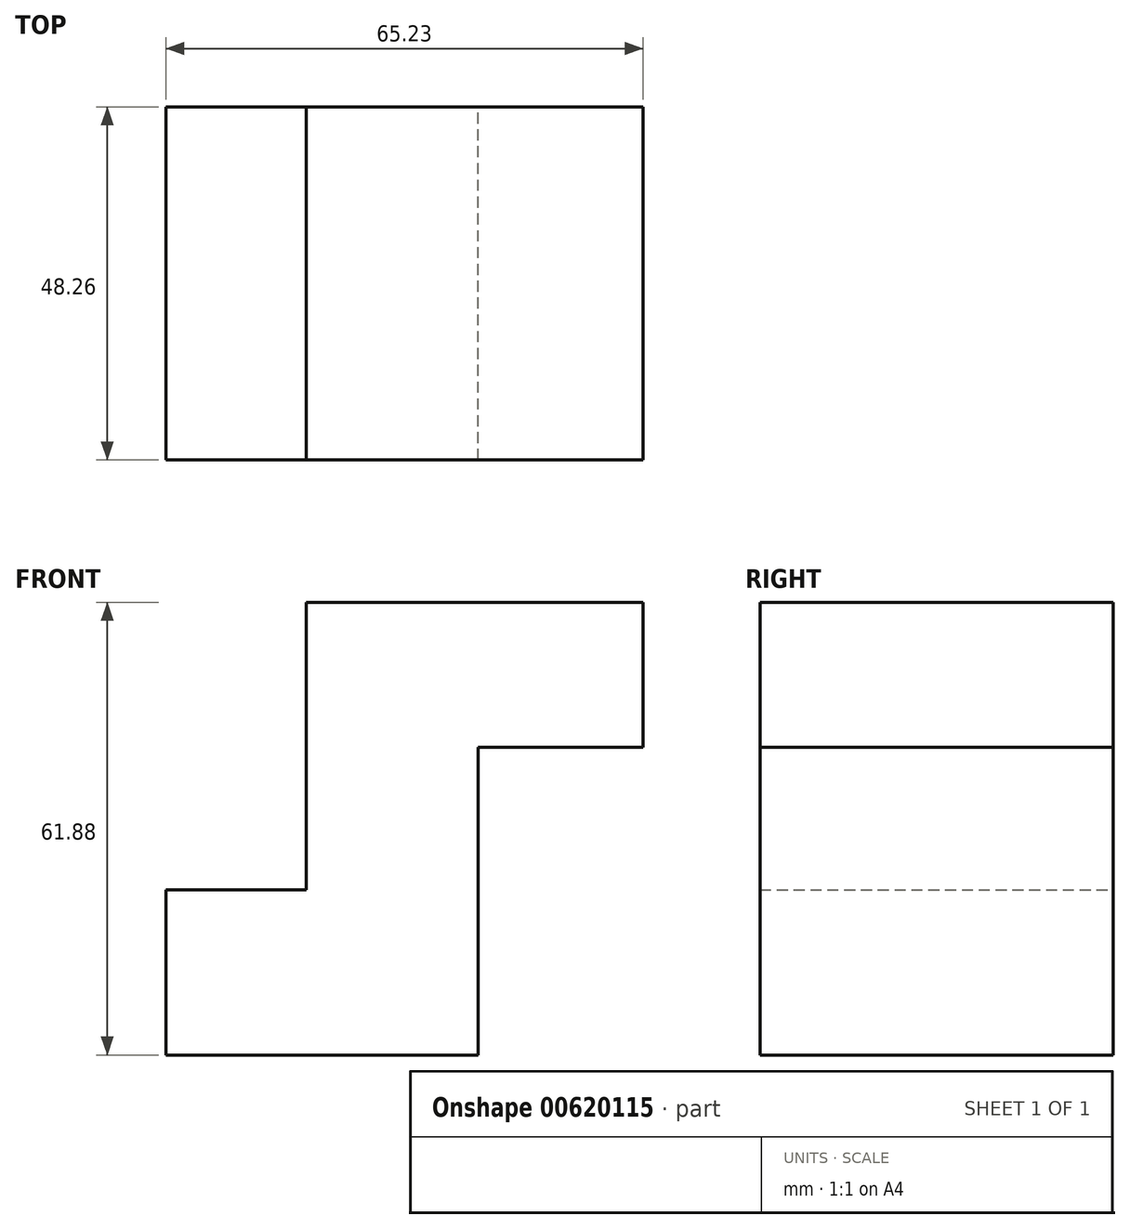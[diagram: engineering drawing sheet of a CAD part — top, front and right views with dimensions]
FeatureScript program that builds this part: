
annotation { "Feature Type Name" : "Feature", "Feature Type Description" : "" }
export const myFeature = defineFeature(function(context is Context, id is Id, definition is map)
    precondition{}
    {
        {
            var Q0;
            Q0=qCreatedBy(makeId("Front.planeOp"),FACE);
            var sketch = newSketch(context, id + "F0", { "sketchPlane" : qUnion([Q0])});
            skLineSegment(sketch, "E0", {"start": v(-52.27, 39.32) * mm, "end": v(-6.25, 39.32) * mm});
            skLineSegment(sketch, "E1", {"start": v(-6.25, 39.32) * mm, "end": v(-6.25, 19.5) * mm});
            skLineSegment(sketch, "E2", {"start": v(-6.25, 19.5) * mm, "end": v(-28.8, 19.5) * mm});
            skLineSegment(sketch, "E3", {"start": v(-28.8, 19.5) * mm, "end": v(-28.8, -22.56) * mm});
            skLineSegment(sketch, "E4", {"start": v(-28.8, -22.56) * mm, "end": v(-71.48, -22.56) * mm});
            skLineSegment(sketch, "E5", {"start": v(-71.48, -22.56) * mm, "end": v(-71.48, 0) * mm});
            skLineSegment(sketch, "E6", {"start": v(-71.48, 0) * mm, "end": v(-52.27, 0) * mm});
            skLineSegment(sketch, "E7", {"start": v(-52.27, 0) * mm, "end": v(-52.27, 39.32) * mm});
            skSolve(sketch);
        }
        {
            var Q0;
            Q0=makeQuery(id+"F0.imprint","IMPRINT",FACE,{"disambiguationData":[TD([[makeQuery(id+"F0.imprint","IMPRINT",EDGE,{"derivedFrom":sQuery(id+"F0.wireOp",EDGE,"E0")}),-1.0]])]});
            extrude(context, id + "F1", {"entities" : qUnion([Q0]), "depth" : 48.26 * mm, "offsetDistance" : 25.4 * mm});
        }
    });
